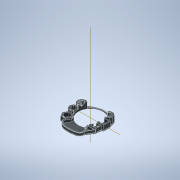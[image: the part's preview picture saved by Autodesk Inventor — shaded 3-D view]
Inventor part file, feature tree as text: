
AUTODESK INVENTOR PART (.ipt)
format: ipt  version: 2022 (Build 260153000, 153)  size: 5,023,232 bytes
history: native  units: mm
features: sketch x27, extrude x26, helix x5, plane x4, fillet x3, revolve x2, pattern_circular x2, chamfer x2
ambient origin geometry x8: Origin, YZ Plane, XZ Plane, XY Plane, X Axis, Y Axis, Z Axis, Center Point
bodies: Solid1 (feature_tree)
feature tree (71):
  revolve  "Revolution1"  [1 undecoded]
  plane  "Work Plane1"
  extrude  "Extrusion4"  Depth=20.0mm
  extrude  "Extrusion2"  Depth=19.0mm
  pattern_circular  "Circular Pattern2"  Count=9  [1 undecoded]
  plane  "Work Plane3"
  extrude  "Extrusion3"  Depth=10.0mm
  pattern_circular  "Circular Pattern3"  Count=7  [1 undecoded]
  helix  "Coil1"  [1 undecoded]
  helix  "Coil2"  [1 undecoded]
  helix  "Coil3"  [1 undecoded]
  helix  "Coil4"  [1 undecoded]
  helix  "Coil5"  [1 undecoded]
  extrude  "Extrusion5"  Depth=20.0mm
  revolve  "Revolution2"  [1 undecoded]
  extrude  "Extrusion6"  Depth=30.0mm
  extrude  "Extrusion15"  Depth=15.0mm
  extrude  "Extrusion16"  Depth=30.0mm
  extrude  "Extrusion17"  Depth=45.0mm
  extrude  "Extrusion18"  Depth=10.0mm
  extrude  "Extrusion19"  Depth=10.0mm
  extrude  "Extrusion20"  Depth=10.0mm
  extrude  "Extrusion21"  Depth=10.0mm
  extrude  "Extrusion22"  Depth=10.0mm
  extrude  "Extrusion23"  Depth=10.0mm
  extrude  "Extrusion25"  Depth=10.0mm TaperAngle=0.0deg
  extrude  "Extrusion26"  Depth=54.0mm TaperAngle=0.0deg
  extrude  "Extrusion27"  Depth=52.0mm
  extrude  "Extrusion28"  Depth=52.0mm
  extrude  "Extrusion29"  Depth=52.0mm
  extrude  "Extrusion30"  Depth=52.0mm
  extrude  "Extrusion31"  Depth=52.0mm
  plane  "Work Plane4"
  extrude  "Extrusion32"  Depth=52.0mm
  extrude  "Extrusion33"  Depth=10.0mm TaperAngle=0.0deg
  chamfer  "Chamfer2"  Distance=5.0mm
  chamfer  "Chamfer3"  Distance=10.0mm
  fillet  "Fillet5"  Radius=15.0mm
  fillet  "Fillet6"  Radius=0.2mm
  extrude  "Extrusion34"  Depth=52.0mm TaperAngle=0.0deg
  fillet  "Fillet16"  Radius=10.0mm
  extrude  "Extrusion35"  Depth=52.0mm TaperAngle=0.0deg
  extrude  "Extrusion36"  Depth=52.0mm TaperAngle=0.0deg
  sketch  "Sketch1"  dims[d11=50.0mm d12=40.0mm]
  sketch  "Sketch3"  dims[d13=20.0mm d14=20.0mm]
  plane  "Work Plane2"
  sketch  "Sketch4"  dims[d15=23.0mm d16=19.0mm d17=90.0mm]
  sketch  "Sketch5"  dims[d18=32.0mm d19=10.0mm]
  sketch  "Sketch7"  dims[d20=151.0mm]
  sketch  "Sketch8"  dims[d26=2.0mm]
  sketch  "Sketch9"  dims[d27=2.0mm]
  sketch  "Sketch10"  dims[d28=2.0mm]
  sketch  "Sketch11"  dims[d29=2.0mm]
  sketch  "Sketch13"  dims[d30=2.0mm]
  sketch  "Sketch16"  dims[d31=90.0deg d32=70.0mm d38=77.75mm d39=0.0mm d40=40.0mm d41=360.0deg d43=70.0mm d44=77.75mm d45=0.0mm d46=40.0mm d47=360.0deg]
  sketch  "Sketch17"  dims[d49=20.0mm d50=20.0mm]
  sketch  "Sketch20"  dims[d51=20.0mm d52=20.0mm]
  sketch  "Sketch21"  dims[d53=40.0mm d54=30.0mm]
  sketch  "Sketch22"  dims[d55=30.0mm d56=15.0mm]
  sketch  "Sketch26"  dims[d57=15.0mm d58=30.0mm]
  sketch  "Sketch27"  dims[d59=77.75mm d60=0.0mm d61=45.0mm]
  sketch  "Sketch28"  dims[d62=35.0mm]
  sketch  "Sketch30"  dims[d63=70.0mm d64=100.0mm d65=10.0mm d66=-0.567232mm d67=90.0deg d68=90.0deg d69=90.0deg d70=90.0deg d71=13.0mm]
  sketch  "Sketch31"  dims[d72=10.0mm d73=39.0mm]
  sketch  "Sketch33"  dims[d74=140.0mm d75=160.0mm d76=10.0mm d77=-0.645772mm d78=90.0deg d79=90.0deg d80=90.0deg d81=90.0deg d82=11.0mm]
  sketch  "Sketch35"  dims[d83=39.0mm d84=10.0mm]
  sketch  "Sketch37"  dims[d85=135.0mm d86=160.0mm d87=10.0mm d88=-0.645772mm d89=90.0deg d90=90.0deg d91=90.0deg d92=90.0deg d93=11.0mm]
  sketch  "Sketch41"  dims[d94=170.0mm d95=160.0mm d96=10.0mm d97=-0.645772mm d98=90.0deg d99=90.0deg d100=90.0deg d101=90.0deg d102=9.0mm]
  sketch  "Sketch43"  dims[d103=170.0mm d104=160.0mm d105=10.0mm d106=-0.645772mm d107=90.0deg d108=90.0deg d109=90.0deg d110=90.0deg d125=3.0mm d126=0.0mm]
  sketch  "Sketch44"  dims[d130=270.0deg d133=54.0mm d134=0.0mm]
  sketch  "Sketch45"  dims[d141=35.0mm d165=35.0mm d166=30.0mm d167=30.0mm d168=30.0mm d169=30.0mm d170=35.0mm d172=35.0mm d186=5.0mm d187=10.0mm d188=0.0mm d190=5.0mm d191=0.0mm d192=10.0mm d193=0.0mm d194=15.0mm d195=0.0mm d196=0.2mm d197=0.0mm d198=5.0mm d199=0.0mm d200=10.0mm d201=0.0mm d202=15.0mm d203=0.0mm d204=3.0mm d205=0.0mm d210=1.0mm d211=0.0mm d213=10.0mm d214=0.0mm d218=30.0mm d219=23.5mm d220=5.75mm d221=5.75mm d222=5.75mm d223=14.0mm d224=0.0mm d225=22.5mm d226=6.25mm d227=6.25mm d228=6.25mm d229=14.0mm d230=0.0mm d235=14.0mm d236=0.0mm d241=10.0mm d242=0.0mm d245=17.5mm d251=10.0mm d252=0.0mm d254=21.0mm d258=24.0mm d259=0.0mm d263=25.0mm d266=5.0mm d267=5.0mm d268=12.0mm d269=0.0mm d270=11.0mm d271=2.0mm d272=45.0deg d273=12.0mm d274=2.0mm d275=45.0deg d276=35.0mm d278=5.0mm d279=5.0mm d280=5.0mm d282=2.0mm d283=1.0mm d292=20.0mm d293=0.0mm d295=2.0mm d299=25.0mm d300=52.0mm d301=54.0mm d302=0.0mm d303=25.0mm d304=5.0mm d305=5.0mm d306=5.0mm d307=5.0mm d308=26.0mm d309=3.0mm d310=2.0mm d311=2.484774mm d312=17.5mm d313=21.0mm d314=0.0mm d315=60.0mm d316=400.0mm d317=0.0mm d132=0.0mm d135=0.0mm]
note: 9 required parameter values undecoded (feature->parameter linkage not recoverable at this tier; creation-order binding heuristic only, values carry confidence <= 0.55)